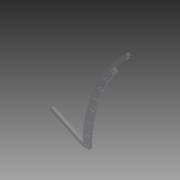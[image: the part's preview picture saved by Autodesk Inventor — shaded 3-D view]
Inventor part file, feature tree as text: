
AUTODESK INVENTOR PART (.ipt)
format: ipt  version: 2013 (Build 170138000, 138)  size: 120,320 bytes
history: native  units: in
note: dims shown in document units (in); Inventor stores cm internally (conversion verified against a paired STEP export)
features: extrude x2, sketch x2, reference x2
ambient origin geometry x8: Origin, YZ Plane, XZ Plane, XY Plane, X Axis, Y Axis, Z Axis, Center Point
bodies: Solid1 (feature_tree)
feature tree (6):
  extrude  "Extrusion1"  TaperAngle=45.0deg  [1 undecoded]
  extrude  "Extrusion2"  Depth=0.25in
  sketch  "Sketch1"  dims[d8=0.25in d9=0.0in d10=45.0deg]
  sketch  "Sketch5"  dims[d11=0.25in d12=0.25in d13=0.1718in d14=0.25in d15=3.0in d16=23.375in d18=0.125in d19=1.75in d20=1.0in d21=0.0in]
  reference  "Reference3"
  reference  "Reference4"
note: 1 required parameter value undecoded (feature->parameter linkage not recoverable at this tier; creation-order binding heuristic only, values carry confidence <= 0.55)
